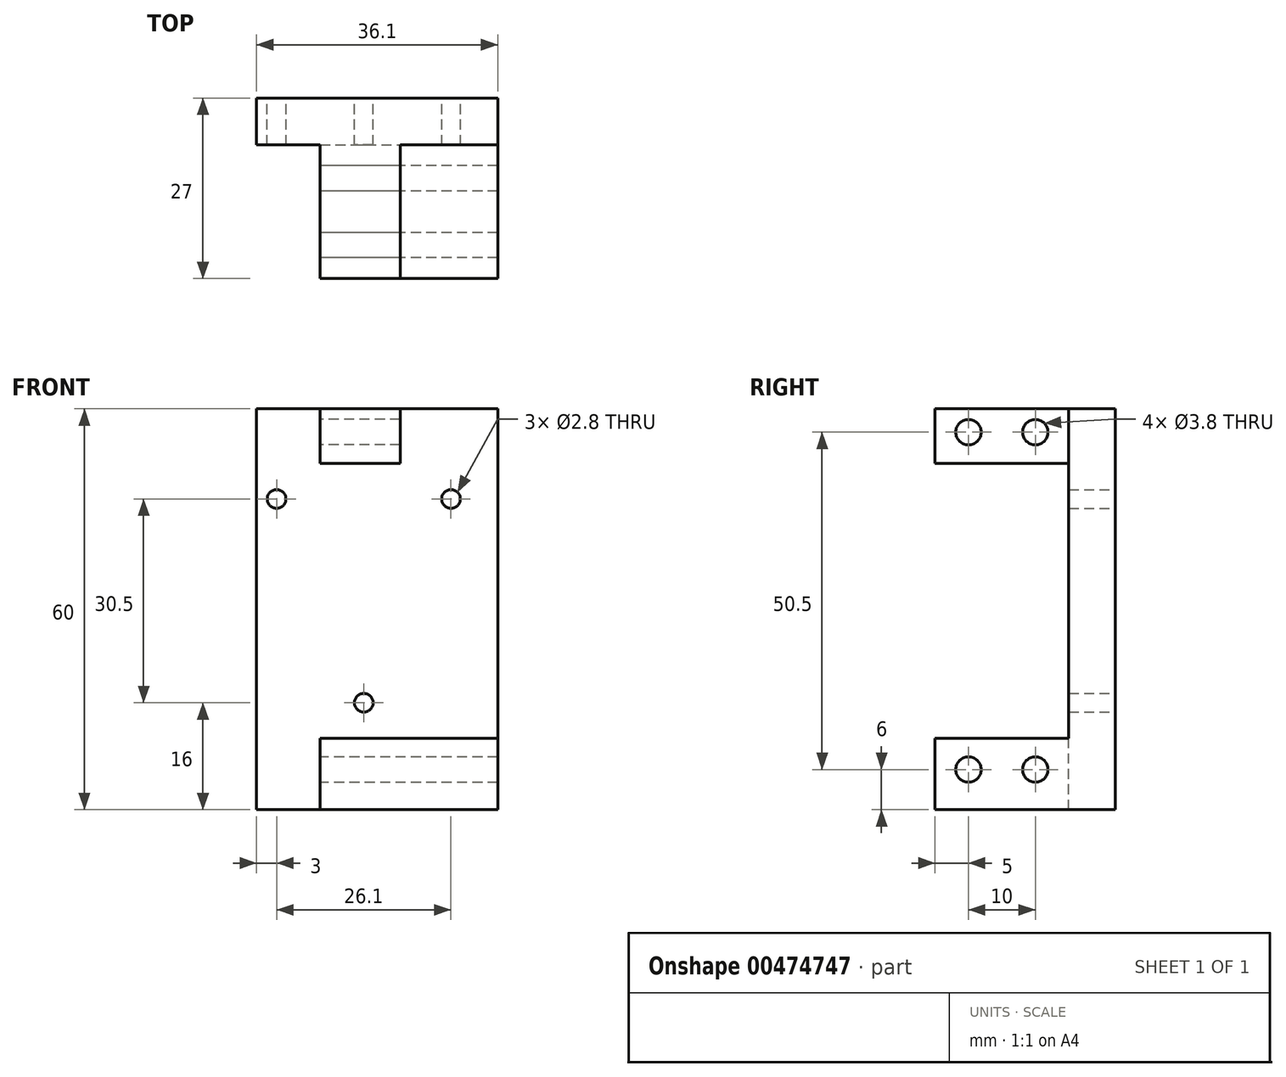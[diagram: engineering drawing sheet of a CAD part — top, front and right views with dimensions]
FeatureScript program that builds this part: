
annotation { "Feature Type Name" : "Feature", "Feature Type Description" : "" }
export const myFeature = defineFeature(function(context is Context, id is Id, definition is map)
    precondition{}
    {
        {
            var Q0;
            Q0=qCreatedBy(makeId("Front.planeOp"),FACE);
            var sketch = newSketch(context, id + "F0", { "sketchPlane" : qUnion([Q0])});
            skLineSegment(sketch, "E0.bottom", {"start": v(0, 40.5) * mm, "end": v(36.1, 40.5) * mm, "construction": true});
            skLineSegment(sketch, "E0.top", {"start": v(0, 0) * mm, "end": v(36.1, 0) * mm, "construction": true});
            skLineSegment(sketch, "E0.left", {"start": v(0, 40.5) * mm, "end": v(0, 0) * mm, "construction": true});
            skLineSegment(sketch, "E0.right", {"start": v(36.1, 40.5) * mm, "end": v(36.1, 0) * mm, "construction": true});
            skLineSegment(sketch, "E1", {"start": v(0, 30.1) * mm, "end": v(42.1, 30.1) * mm, "construction": true});
            skLineSegment(sketch, "E2", {"start": v(42.1, 50.1) * mm, "end": v(40.1, 50.1) * mm, "construction": true});
            skLineSegment(sketch, "E3", {"start": v(42.1, 50.1) * mm, "end": v(42.1, 10.1) * mm, "construction": true});
            skLineSegment(sketch, "E4", {"start": v(42.1, 10.1) * mm, "end": v(40.1, 10.1) * mm, "construction": true});
            skLineSegment(sketch, "E5", {"start": v(40.1, 10.1) * mm, "end": v(40.1, 50.1) * mm, "construction": true});
            skLineSegment(sketch, "E6", {"start": v(26.6, 40.5) * mm, "end": v(26.6, 48) * mm, "construction": true});
            skLineSegment(sketch, "E7", {"start": v(26.6, 48) * mm, "end": v(29.1, 48) * mm, "construction": true});
            skLineSegment(sketch, "E8", {"start": v(29.1, 48) * mm, "end": v(29.1, 40.5) * mm, "construction": true});
            skLineSegment(sketch, "E9", {"start": v(26.6, 0) * mm, "end": v(26.6, -7.5) * mm, "construction": true});
            skLineSegment(sketch, "E10", {"start": v(26.6, -7.5) * mm, "end": v(29.1, -7.5) * mm, "construction": true});
            skLineSegment(sketch, "E11", {"start": v(29.1, -7.5) * mm, "end": v(29.1, 0) * mm, "construction": true});
            skCircle(sketch, "E12", {"center": v(5, 35.5) * mm, "radius": 1.4 * mm});
            skCircle(sketch, "E13", {"center": v(31.1, 35.5) * mm, "radius": 1.4 * mm});
            skLineSegment(sketch, "E14", {"start": v(5, 35.5) * mm, "end": v(31.1, 35.5) * mm, "construction": true});
            skCircle(sketch, "E15", {"center": v(18.05, 5) * mm, "radius": 1.4 * mm});
            skLineSegment(sketch, "E16.top", {"start": v(0, -11) * mm, "end": v(36.1, -11) * mm});
            skLineSegment(sketch, "E17", {"start": v(0, -11) * mm, "end": v(0, 49) * mm});
            skLineSegment(sketch, "E18", {"start": v(0, 49) * mm, "end": v(36.1, 49) * mm});
            skLineSegment(sketch, "E19", {"start": v(36.1, 49) * mm, "end": v(36.1, -11) * mm});
            skLineSegment(sketch, "E20", {"start": v(18.05, 5) * mm, "end": v(18.05, 35.5) * mm, "construction": true});
            skSolve(sketch);
        }
        {
            var Q0;
            Q0 = qSketchRegion(id + "F0", true);
            extrude(context, id + "F1", {"entities" : qUnion([Q0]), "depth" : 7 * mm, "offsetDistance" : 25 * mm});
        }
        {
            var Q0;
            Q0=makeQuery(id+"F1.opExtrude","CAP_FACE",FACE,{"disambiguationData":[OSD([sQuery(id+"F0.wireOp",EDGE,"E12"),sQuery(id+"F0.wireOp",EDGE,"E13"),sQuery(id+"F0.wireOp",EDGE,"E15"),sQuery(id+"F0.wireOp",EDGE,"E16.top"),sQuery(id+"F0.wireOp",EDGE,"E17"),sQuery(id+"F0.wireOp",EDGE,"E18"),sQuery(id+"F0.wireOp",EDGE,"E19")])],"isStart":false});
            var sketch = newSketch(context, id + "F2", { "sketchPlane" : qUnion([Q0])});
            skLineSegment(sketch, "E21.bottom", {"start": v(11.5, -11) * mm, "end": v(36.1, -11) * mm});
            skLineSegment(sketch, "E21.top", {"start": v(11.5, -0.3) * mm, "end": v(36.1, -0.3) * mm});
            skLineSegment(sketch, "E21.left", {"start": v(11.5, -11) * mm, "end": v(11.5, -0.3) * mm});
            skLineSegment(sketch, "E21.right", {"start": v(36.1, -11) * mm, "end": v(36.1, -0.3) * mm});
            skLineSegment(sketch, "E22.top", {"start": v(11.5, 40.8) * mm, "end": v(23.5, 40.8) * mm});
            skLineSegment(sketch, "E22.right", {"start": v(23.5, 49) * mm, "end": v(23.5, 40.8) * mm});
            skLineSegment(sketch, "E23", {"start": v(11.5, 40.8) * mm, "end": v(11.5, 49) * mm});
            skLineSegment(sketch, "E24", {"start": v(11.5, 49) * mm, "end": v(23.5, 49) * mm});
            skSolve(sketch);
        }
        {
            var Q0;
            Q0 = qSketchRegion(id + "F2", true);
            extrude(context, id + "F3", {"entities" : qUnion([Q0]), "operationType" : NewBodyOperationType.ADD, "depth" : 20 * mm, "offsetDistance" : 25 * mm});
        }
        {
            var Q0;
            Q0=makeQuery(id+"F3.opExtrude","SWEPT_FACE",FACE,{"disambiguationData":[OSD([sQuery(id+"F2.wireOp",EDGE,"E23")])]});
            var sketch = newSketch(context, id + "F4", { "sketchPlane" : qUnion([Q0])});
            skCircle(sketch, "E25", {"center": v(12, 45.5) * mm, "radius": 1.9 * mm});
            skCircle(sketch, "E26", {"center": v(22, 45.5) * mm, "radius": 1.9 * mm});
            skCircle(sketch, "E27", {"center": v(12, -5) * mm, "radius": 1.9 * mm});
            skCircle(sketch, "E28", {"center": v(22, -5) * mm, "radius": 1.9 * mm});
            skLineSegment(sketch, "E29", {"start": v(12, 45.5) * mm, "end": v(22, 45.5) * mm, "construction": true});
            skLineSegment(sketch, "E30", {"start": v(17, 49) * mm, "end": v(17, 40.8) * mm, "construction": true});
            skLineSegment(sketch, "E31", {"start": v(17, -0.3) * mm, "end": v(17, -11) * mm, "construction": true});
            skLineSegment(sketch, "E32", {"start": v(12, -5) * mm, "end": v(22, -5) * mm, "construction": true});
            skSolve(sketch);
        }
        {
            var Q0;
            Q0 = qSketchRegion(id + "F4", true);
            var Q1;
            Q1=makeQuery(id+"F3.boolean.opBoolean","MERGE",FACE,{"derivedFrom":[makeQuery(id+"F1.opExtrude","SWEPT_FACE",FACE,{"disambiguationData":[OSD([sQuery(id+"F0.wireOp",EDGE,"E19")])]}),makeQuery(id+"F3.opExtrude","SWEPT_FACE",FACE,{"disambiguationData":[OSD([sQuery(id+"F2.wireOp",EDGE,"E21.right")])]})]});
            extrude(context, id + "F5", {"entities" : qUnion([Q0]), "operationType" : NewBodyOperationType.REMOVE, "endBound" : BoundingType.UP_TO_SURFACE, "oppositeDirection" : true, "depth" : 25 * mm, "endBoundEntityFace" : qUnion([Q1]), "offsetDistance" : 25 * mm});
        }
        {
            var Q0;
            Q0=makeQuery(id+"F3.boolean.opBoolean","MERGE",FACE,{"derivedFrom":[makeQuery(id+"F1.opExtrude","SWEPT_FACE",FACE,{"disambiguationData":[OSD([sQuery(id+"F0.wireOp",EDGE,"E19")])]}),makeQuery(id+"F3.opExtrude","SWEPT_FACE",FACE,{"disambiguationData":[OSD([sQuery(id+"F2.wireOp",EDGE,"E21.right")])]})]});
            var sketch = newSketch(context, id + "F6", { "sketchPlane" : qUnion([Q0])});
            skLineSegment(sketch, "E33", {"start": v(-27, -0.3) * mm, "end": v(-27, -11) * mm});
            skLineSegment(sketch, "E34", {"start": v(-27, -11) * mm, "end": v(0, -11) * mm});
            skLineSegment(sketch, "E35", {"start": v(0, -11) * mm, "end": v(0, 49) * mm});
            skLineSegment(sketch, "E36", {"start": v(0, 49) * mm, "end": v(-7, 49) * mm});
            skLineSegment(sketch, "E37", {"start": v(-7, 49) * mm, "end": v(-7, -0.3) * mm});
            skLineSegment(sketch, "E38", {"start": v(-7, -0.3) * mm, "end": v(-27, -0.3) * mm});
            skCircle(sketch, "E39", {"center": v(-22, -5) * mm, "radius": 1.9 * mm});
            skCircle(sketch, "E40", {"center": v(-12, -5) * mm, "radius": 1.9 * mm});
            skSolve(sketch);
        }
        {
            var Q0;
            Q0 = qSketchRegion(id + "F6", true);
            extrude(context, id + "F7", {"entities" : qUnion([Q0]), "operationType" : NewBodyOperationType.ADD, "depth" : 2 * mm, "offsetDistance" : 25 * mm});
        }
        {
            var Q0;
            Q0=makeQuery(id+"F1.opExtrude","SWEPT_FACE",FACE,{"disambiguationData":[OSD([sQuery(id+"F0.wireOp",EDGE,"E17")])]});
            var sketch = newSketch(context, id + "F8", { "sketchPlane" : qUnion([Q0])});
            skLineSegment(sketch, "E41.bottom", {"start": v(7, 49) * mm, "end": v(0, 49) * mm});
            skLineSegment(sketch, "E41.top", {"start": v(7, -11) * mm, "end": v(0, -11) * mm});
            skLineSegment(sketch, "E41.left", {"start": v(7, 49) * mm, "end": v(7, -11) * mm});
            skLineSegment(sketch, "E41.right", {"start": v(0, 49) * mm, "end": v(0, -11) * mm});
            skSolve(sketch);
        }
        {
            var Q0;
            Q0 = qSketchRegion(id + "F8", true);
            extrude(context, id + "F9", {"entities" : qUnion([Q0]), "operationType" : NewBodyOperationType.REMOVE, "oppositeDirection" : true, "depth" : 2 * mm, "offsetDistance" : 25 * mm});
        }
    });
